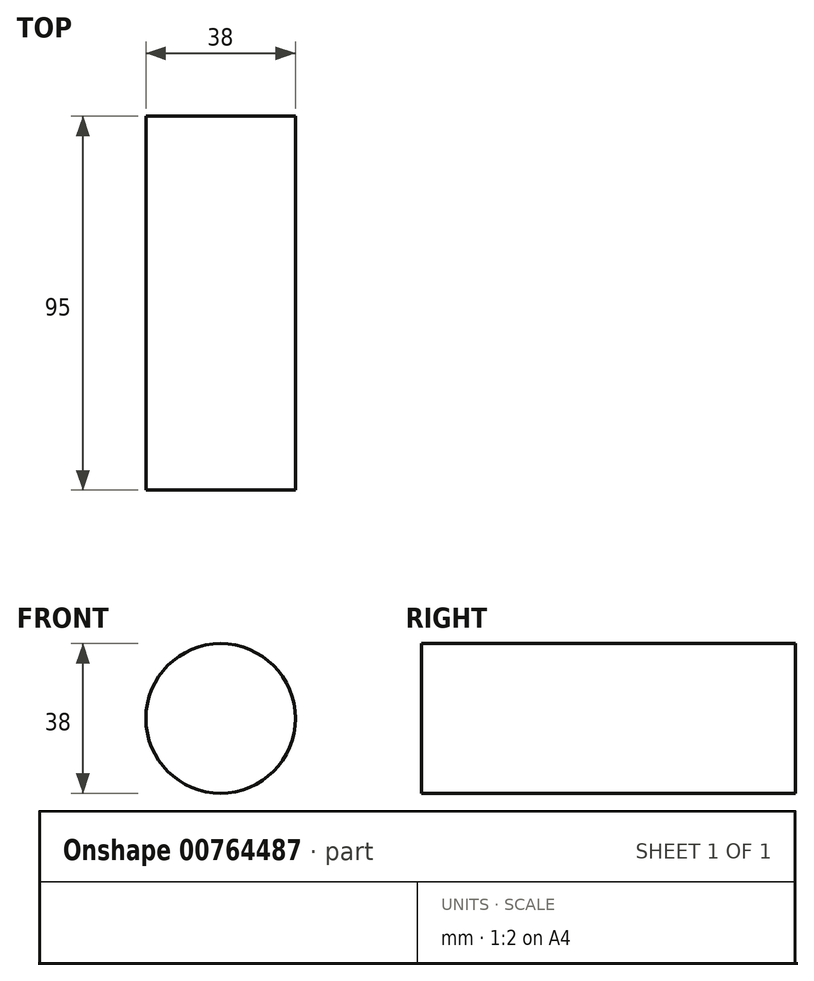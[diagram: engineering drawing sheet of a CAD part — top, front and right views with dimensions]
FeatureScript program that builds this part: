
annotation { "Feature Type Name" : "Feature", "Feature Type Description" : "" }
export const myFeature = defineFeature(function(context is Context, id is Id, definition is map)
    precondition{}
    {
        {
            var Q0;
            Q0=qCreatedBy(makeId("Front.planeOp"),FACE);
            var sketch = newSketch(context, id + "F0", { "sketchPlane" : qUnion([Q0])});
            skCircle(sketch, "E0", {"center": v(0, 0) * mm, "radius": 19 * mm});
            skSolve(sketch);
        }
        {
            var Q0;
            Q0=makeQuery(id+"F0.imprint","IMPRINT",FACE,{"disambiguationData":[TD([[makeQuery(id+"F0.imprint","IMPRINT",EDGE,{"derivedFrom":sQuery(id+"F0.wireOp",EDGE,"E0")}),1.0]])]});
            extrude(context, id + "F1", {"entities" : qUnion([Q0]), "depth" : 95 * mm, "offsetDistance" : 25 * mm});
        }
    });
